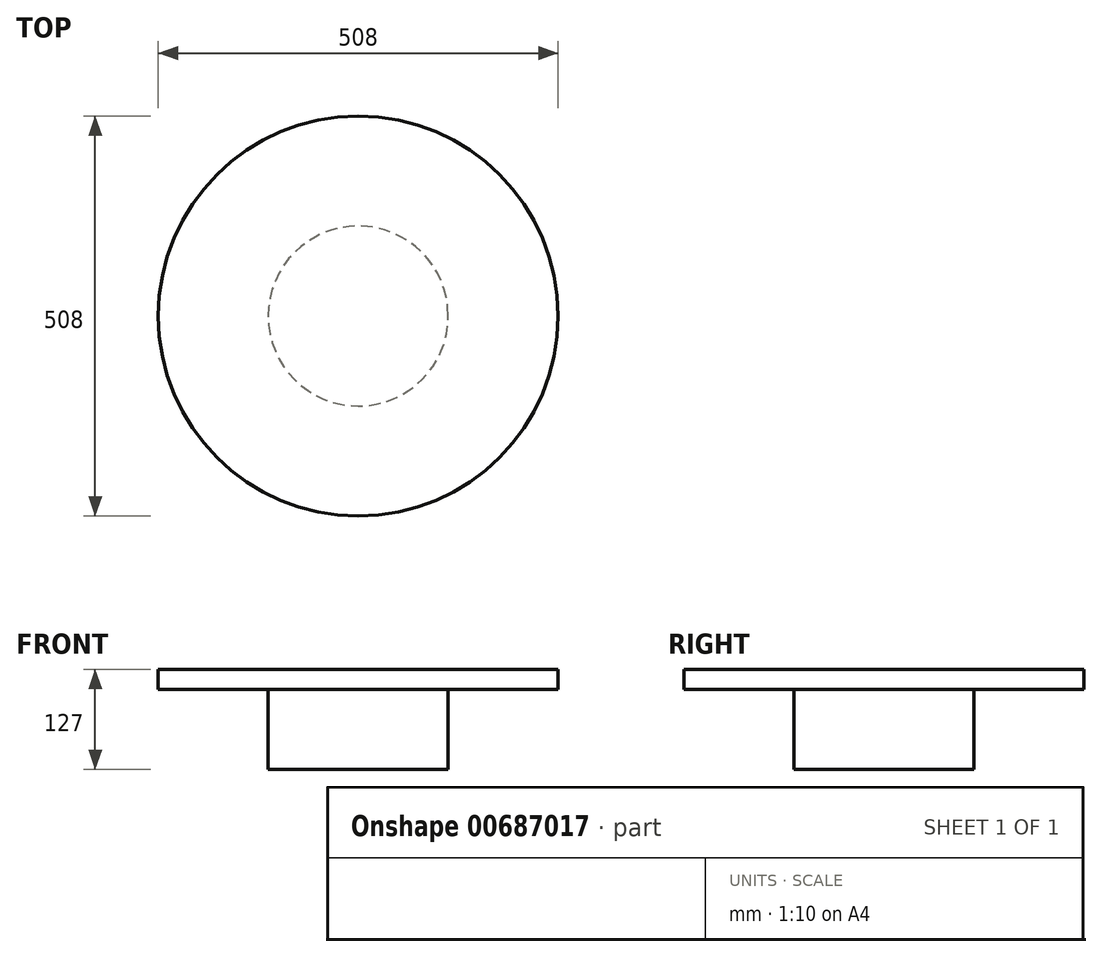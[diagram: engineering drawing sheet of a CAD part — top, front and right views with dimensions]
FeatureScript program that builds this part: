
annotation { "Feature Type Name" : "Feature", "Feature Type Description" : "" }
export const myFeature = defineFeature(function(context is Context, id is Id, definition is map)
    precondition{}
    {
        {
            var Q0;
            Q0=qCreatedBy(makeId("Top.planeOp"),FACE);
            var sketch = newSketch(context, id + "F0", { "sketchPlane" : qUnion([Q0])});
            skCircle(sketch, "E0", {"center": v(0, 0) * mm, "radius": 114.3 * mm});
            skSolve(sketch);
        }
        {
            var Q0;
            Q0 = qSketchRegion(id + "F0", true);
            extrude(context, id + "F1", {"entities" : qUnion([Q0]), "oppositeDirection" : true, "depth" : 127 * mm, "offsetDistance" : 25.4 * mm});
        }
        {
            var Q0;
            Q0=qCreatedBy(makeId("Top.planeOp"),FACE);
            var sketch = newSketch(context, id + "F2", { "sketchPlane" : qUnion([Q0])});
            skCircle(sketch, "E1", {"center": v(0, 0) * mm, "radius": 254 * mm});
            skSolve(sketch);
        }
        {
            var Q0;
            Q0 = qSketchRegion(id + "F2", true);
            extrude(context, id + "F3", {"entities" : qUnion([Q0]), "operationType" : NewBodyOperationType.ADD, "oppositeDirection" : true, "depth" : 25.4 * mm, "offsetDistance" : 25.4 * mm});
        }
    });
